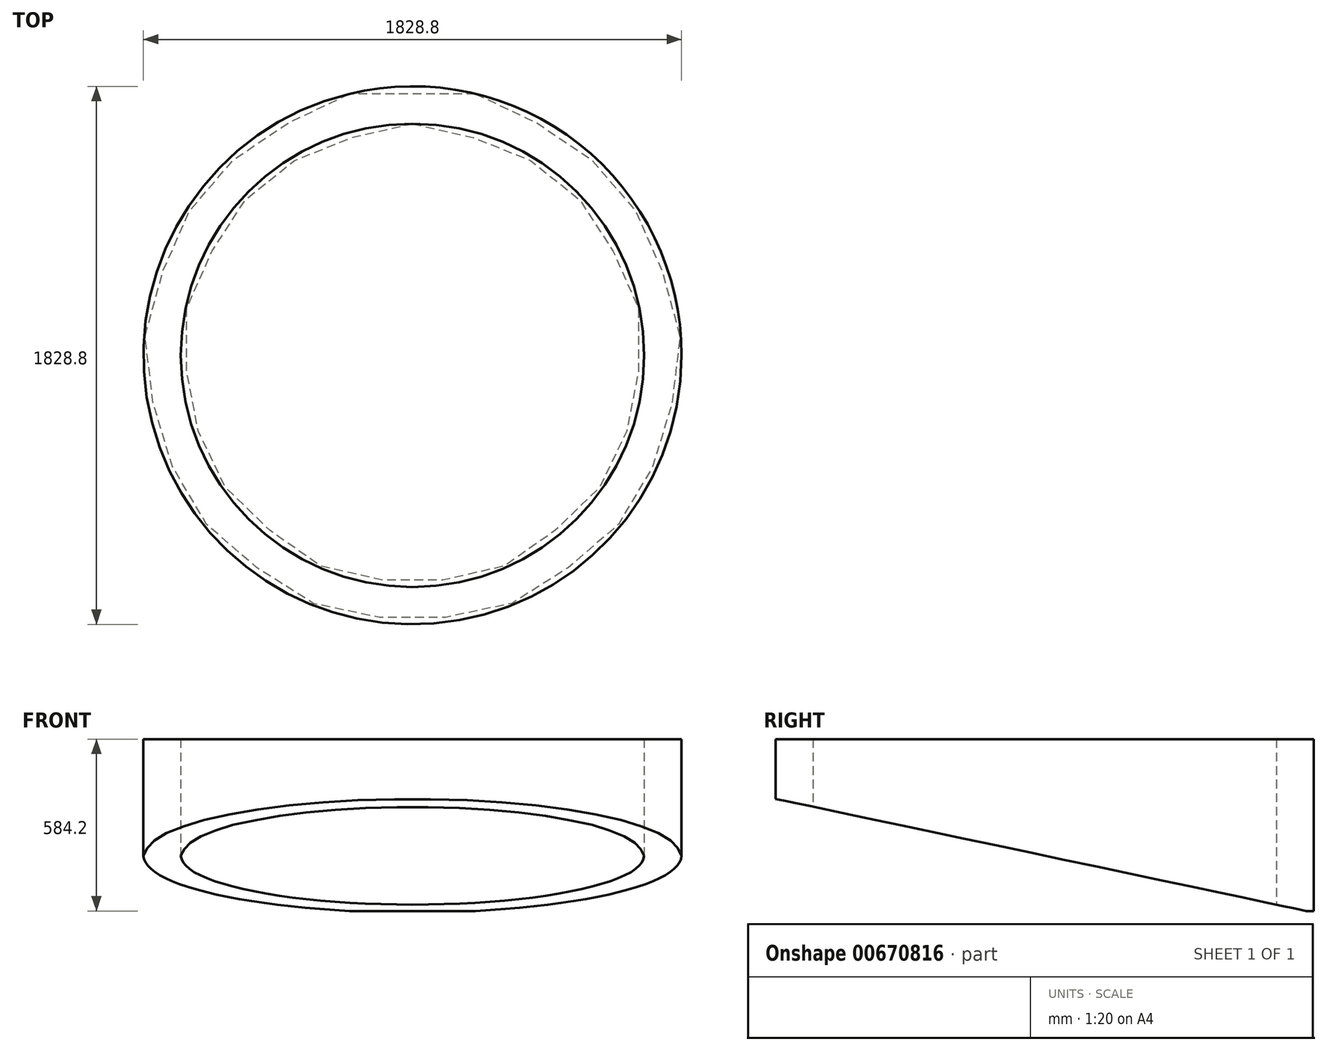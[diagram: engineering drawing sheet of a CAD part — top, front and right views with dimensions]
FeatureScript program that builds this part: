
annotation { "Feature Type Name" : "Feature", "Feature Type Description" : "" }
export const myFeature = defineFeature(function(context is Context, id is Id, definition is map)
    precondition{}
    {
        {
            var Q0;
            Q0=qCreatedBy(makeId("Top.planeOp"),FACE);
            var sketch = newSketch(context, id + "F0", { "sketchPlane" : qUnion([Q0])});
            skCircle(sketch, "E0", {"center": v(0, 0) * mm, "radius": 914.4 * mm});
            skCircle(sketch, "E1", {"center": v(0, 0) * mm, "radius": 787.4 * mm});
            skSolve(sketch);
        }
        {
            var Q0;
            Q0=makeQuery(id+"F0.imprint","IMPRINT",FACE,{"disambiguationData":[TD([[makeQuery(id+"F0.imprint","IMPRINT",EDGE,{"derivedFrom":sQuery(id+"F0.wireOp",EDGE,"E0")}),1.0]])]});
            extrude(context, id + "F1", {"entities" : qUnion([Q0]), "depth" : 584.2 * mm, "offsetDistance" : 25.4 * mm});
        }
        {
            var Q0;
            Q0=qCreatedBy(makeId("Right.planeOp"),FACE);
            var sketch = newSketch(context, id + "F2", { "sketchPlane" : qUnion([Q0])});
            skLineSegment(sketch, "E2", {"start": v(889, 0) * mm, "end": v(-914.4, 381) * mm});
            skLineSegment(sketch, "E3", {"start": v(-914.4, 381) * mm, "end": v(-914.4, 0) * mm});
            skLineSegment(sketch, "E4", {"start": v(-914.4, 0) * mm, "end": v(889, 0) * mm});
            skLineSegment(sketch, "E5", {"start": v(914.4, 584.2) * mm, "end": v(914.4, 0) * mm});
            skLineSegment(sketch, "E6", {"start": v(-914.4, 0) * mm, "end": v(-914.4, 490.27) * mm, "construction": true});
            skLineSegment(sketch, "E7", {"start": v(914.4, 584.2) * mm, "end": v(914.4, 0) * mm, "construction": true});
            skSolve(sketch);
        }
        {
            var Q0;
            Q0=makeQuery(id+"F2.imprint","IMPRINT",FACE,{"disambiguationData":[TD([[makeQuery(id+"F2.imprint","IMPRINT",EDGE,{"derivedFrom":sQuery(id+"F2.wireOp",EDGE,"E2")}),1.0]])]});
            extrude(context, id + "F3", {"entities" : qUnion([Q0]), "operationType" : NewBodyOperationType.REMOVE, "endBound" : BoundingType.THROUGH_ALL, "depth" : 25.4 * mm, "offsetDistance" : 25.4 * mm, "hasSecondDirection" : true, "secondDirectionBound" : BoundingType.THROUGH_ALL, "secondDirectionOppositeDirection" : true, "secondDirectionDepth" : 25.4 * mm});
        }
    });
